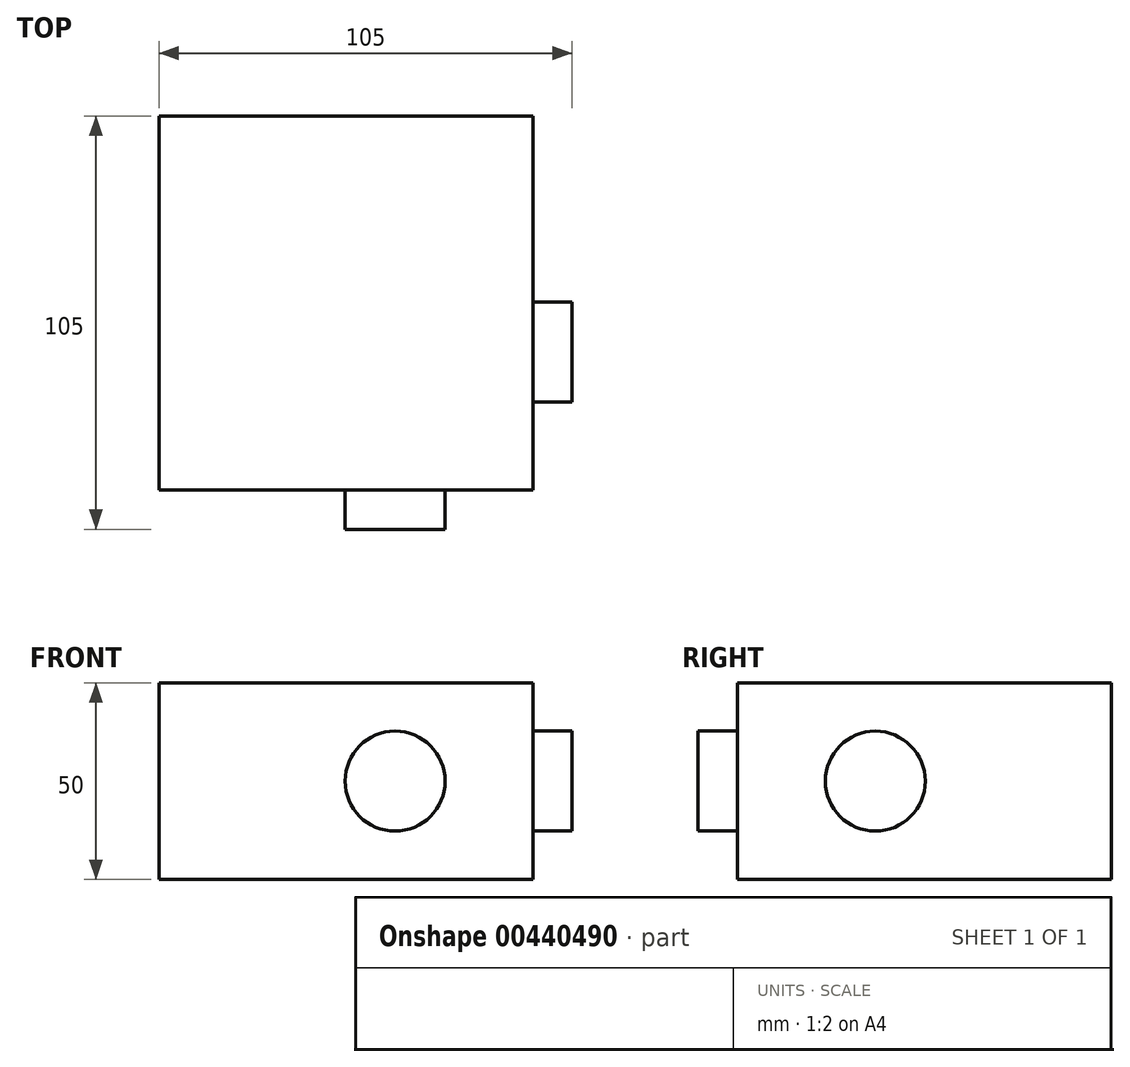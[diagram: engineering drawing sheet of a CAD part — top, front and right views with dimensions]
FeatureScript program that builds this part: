
annotation { "Feature Type Name" : "Feature", "Feature Type Description" : "" }
export const myFeature = defineFeature(function(context is Context, id is Id, definition is map)
    precondition{}
    {
        {
            var Q0;
            Q0=qCreatedBy(makeId("Top.planeOp"),FACE);
            var sketch = newSketch(context, id + "F0", { "sketchPlane" : qUnion([Q0])});
            skLineSegment(sketch, "E0.bottom", {"start": v(-47.5, -47.5) * mm, "end": v(47.5, -47.5) * mm});
            skLineSegment(sketch, "E0.top", {"start": v(-47.5, 47.5) * mm, "end": v(47.5, 47.5) * mm});
            skLineSegment(sketch, "E0.left", {"start": v(-47.5, -47.5) * mm, "end": v(-47.5, 47.5) * mm});
            skLineSegment(sketch, "E0.right", {"start": v(47.5, -47.5) * mm, "end": v(47.5, 47.5) * mm});
            skPoint(sketch, "E0.middle", {"position": v(0, 0) * mm});
            skSolve(sketch);
        }
        {
            var Q0;
            Q0 = qSketchRegion(id + "F0", true);
            extrude(context, id + "F1", {"entities" : qUnion([Q0]), "depth" : 50 * mm});
        }
        {
            var Q0;
            Q0=makeQuery(id+"F1.opExtrude","SWEPT_FACE",FACE,{"disambiguationData":[OSD([sQuery(id+"F0.wireOp",EDGE,"E0.bottom")])]});
            var sketch = newSketch(context, id + "F2", { "sketchPlane" : qUnion([Q0])});
            skCircle(sketch, "E1", {"center": v(12.5, 25) * mm, "radius": 12.7 * mm});
            skSolve(sketch);
        }
        {
            var Q0;
            Q0 = qSketchRegion(id + "F2", true);
            extrude(context, id + "F3", {"entities" : qUnion([Q0]), "operationType" : NewBodyOperationType.ADD, "depth" : 10 * mm, "offsetDistance" : 25 * mm});
        }
        {
            var Q0;
            Q0=makeQuery(id+"F1.opExtrude","SWEPT_FACE",FACE,{"disambiguationData":[OSD([sQuery(id+"F0.wireOp",EDGE,"E0.right")])]});
            var sketch = newSketch(context, id + "F4", { "sketchPlane" : qUnion([Q0])});
            skCircle(sketch, "E2", {"center": v(-12.5, 25) * mm, "radius": 12.7 * mm});
            skSolve(sketch);
        }
        {
            var Q0;
            Q0 = qSketchRegion(id + "F4", true);
            extrude(context, id + "F5", {"entities" : qUnion([Q0]), "operationType" : NewBodyOperationType.ADD, "depth" : 10 * mm, "offsetDistance" : 25 * mm});
        }
    });
